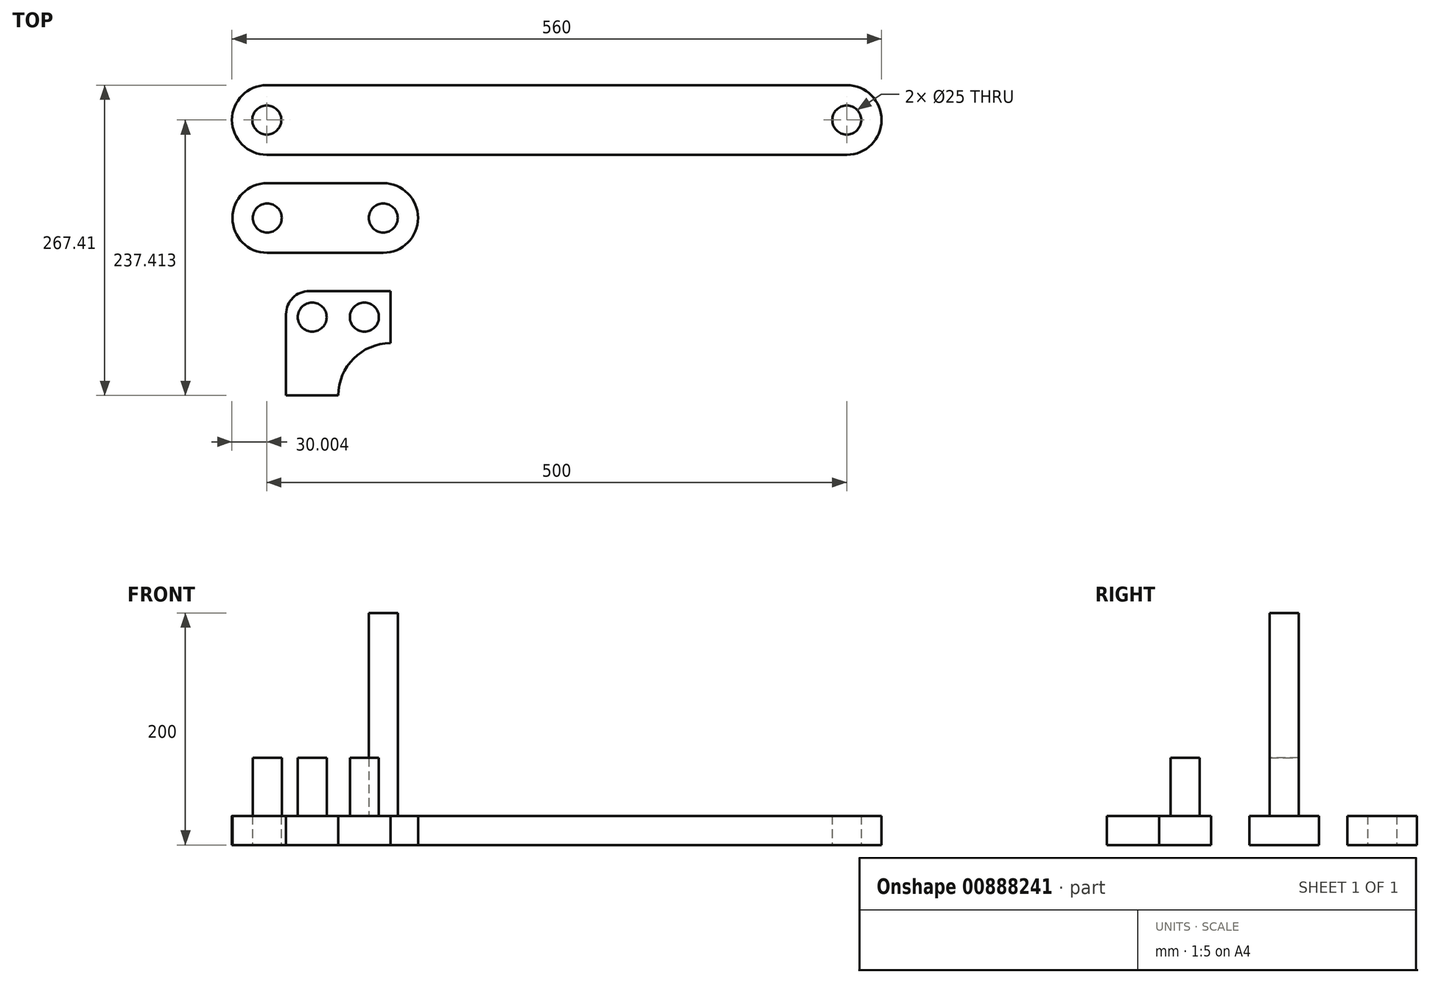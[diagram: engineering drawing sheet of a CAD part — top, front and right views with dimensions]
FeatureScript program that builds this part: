
annotation { "Feature Type Name" : "Feature", "Feature Type Description" : "" }
export const myFeature = defineFeature(function(context is Context, id is Id, definition is map)
    precondition{}
    {
        {
            var Q0;
            Q0=qCreatedBy(makeId("Top.planeOp"),FACE);
            var sketch = newSketch(context, id + "F0", { "sketchPlane" : qUnion([Q0])});
            skLineSegment(sketch, "E0.bottom", {"start": v(50, 30) * mm, "end": v(-50, 30) * mm});
            skLineSegment(sketch, "E0.top", {"start": v(50, -30) * mm, "end": v(-50, -30) * mm});
            skPoint(sketch, "E0.middle", {"position": v(0, 0) * mm});
            skPoint(sketch, "E1.center.orphan", {"position": v(-50, 0) * mm});
            skPoint(sketch, "E2.center.orphan", {"position": v(50, 0) * mm});
            skArc(sketch, "E3", {"start": v(-50, 30) * mm, "mid": v(-80, 0) * mm, "end": v(-50, -30) * mm});
            skArc(sketch, "E4", {"start": v(50, -30) * mm, "mid": v(80, 0) * mm, "end": v(50, 30) * mm});
            skCircle(sketch, "E5", {"center": v(-50, 0) * mm, "radius": 12.5 * mm});
            skCircle(sketch, "E6", {"center": v(50, 0) * mm, "radius": 12.5 * mm});
            skLineSegment(sketch, "E7.bottom", {"start": v(56.26, -62.93) * mm, "end": v(-33.74, -62.93) * mm});
            skLineSegment(sketch, "E7.top", {"start": v(56.26, -107.93) * mm, "end": v(11.26, -107.93) * mm});
            skLineSegment(sketch, "E7.left", {"start": v(56.26, -62.93) * mm, "end": v(56.26, -107.93) * mm});
            skLineSegment(sketch, "E8.top", {"start": v(11.26, -152.93) * mm, "end": v(-33.74, -152.93) * mm});
            skLineSegment(sketch, "E8.left", {"start": v(11.26, -107.93) * mm, "end": v(11.26, -152.93) * mm});
            skLineSegment(sketch, "E9", {"start": v(-33.74, -62.93) * mm, "end": v(-33.74, -152.93) * mm});
            skPoint(sketch, "E10.centerSnap0", {"position": v(-11.24, -152.93) * mm});
            skPoint(sketch, "E10.centerSnap1", {"position": v(11.26, -130.43) * mm});
            skCircle(sketch, "E11", {"center": v(33.76, -85.43) * mm, "radius": 12.5 * mm});
            skPoint(sketch, "E11.centerSnap0", {"position": v(56.26, -85.43) * mm});
            skPoint(sketch, "E11.centerSnap1", {"position": v(33.76, -107.93) * mm});
            skCircle(sketch, "E12", {"center": v(-11.24, -85.43) * mm, "radius": 12.5 * mm});
            skLineSegment(sketch, "E13.bottom", {"start": v(449.6, 114.48) * mm, "end": v(-50.4, 114.48) * mm});
            skLineSegment(sketch, "E13.top", {"start": v(449.6, 54.48) * mm, "end": v(-50.4, 54.48) * mm});
            skPoint(sketch, "E13.middle", {"position": v(199.6, 84.48) * mm});
            skPoint(sketch, "E14.center.orphan", {"position": v(-50.4, 84.48) * mm});
            skPoint(sketch, "E15.center.orphan", {"position": v(449.6, 84.48) * mm});
            skArc(sketch, "E16", {"start": v(-50.4, 114.48) * mm, "mid": v(-80.4, 84.48) * mm, "end": v(-50.4, 54.48) * mm});
            skArc(sketch, "E17", {"start": v(449.6, 54.48) * mm, "mid": v(479.6, 84.48) * mm, "end": v(449.6, 114.48) * mm});
            skCircle(sketch, "E18", {"center": v(-50.4, 84.48) * mm, "radius": 12.5 * mm});
            skCircle(sketch, "E19", {"center": v(449.6, 84.48) * mm, "radius": 12.5 * mm});
            skSolve(sketch);
        }
        {
            var Q0;
            Q0=makeQuery(id+"F0.imprint","IMPRINT",FACE,{"disambiguationData":[TD([[makeQuery(id+"F0.imprint","IMPRINT",EDGE,{"derivedFrom":sQuery(id+"F0.wireOp",EDGE,"E0.bottom")}),1.0]])]});
            extrude(context, id + "F1", {"entities" : qUnion([Q0]), "depth" : 25 * mm, "offsetDistance" : 25 * mm});
        }
        {
            var Q0;
            Q0=makeQuery(id+"F0.imprint","IMPRINT",FACE,{"disambiguationData":[TD([[makeQuery(id+"F0.imprint","IMPRINT",EDGE,{"derivedFrom":sQuery(id+"F0.wireOp",EDGE,"E6")}),1.0]])]});
            extrude(context, id + "F2", {"entities" : qUnion([Q0]), "operationType" : NewBodyOperationType.ADD, "depth" : 200 * mm, "offsetDistance" : 25 * mm});
        }
        {
            var Q0;
            Q0=makeQuery(id+"F0.imprint","IMPRINT",FACE,{"disambiguationData":[TD([[makeQuery(id+"F0.imprint","IMPRINT",EDGE,{"derivedFrom":sQuery(id+"F0.wireOp",EDGE,"E5")}),1.0]])]});
            extrude(context, id + "F3", {"entities" : qUnion([Q0]), "operationType" : NewBodyOperationType.ADD, "depth" : 75 * mm, "offsetDistance" : 25 * mm});
        }
        {
            var Q0;
            Q0=makeQuery(id+"F0.imprint","IMPRINT",FACE,{"disambiguationData":[TD([[makeQuery(id+"F0.imprint","IMPRINT",EDGE,{"derivedFrom":sQuery(id+"F0.wireOp",EDGE,"E7.bottom")}),1.0]])]});
            extrude(context, id + "F4", {"entities" : qUnion([Q0]), "depth" : 25 * mm, "offsetDistance" : 25 * mm});
        }
        {
            var Q0;
            Q0=makeQuery(id+"F4.opExtrude","SWEPT_EDGE",EDGE,{"disambiguationData":[OSD([sQuery(id+"F0.wireOp",EDGE,"E7.top"),sQuery(id+"F0.wireOp",EDGE,"E8.left")])]});
            fillet(context, id + "F5", {"entities" : qUnion([Q0]), "radius" : 45 * mm, "tangentPropagation" : true, "allowEdgeOverflow" : false});
        }
        {
            var Q0;
            Q0=makeQuery(id+"F4.opExtrude","SWEPT_EDGE",EDGE,{"disambiguationData":[OSD([sQuery(id+"F0.wireOp",EDGE,"E7.bottom"),sQuery(id+"F0.wireOp",EDGE,"E9")])]});
            fillet(context, id + "F6", {"entities" : qUnion([Q0]), "radius" : 20 * mm, "tangentPropagation" : true, "allowEdgeOverflow" : false});
        }
        {
            var Q0;
            Q0=makeQuery(id+"F0.imprint","IMPRINT",FACE,{"disambiguationData":[TD([[makeQuery(id+"F0.imprint","IMPRINT",EDGE,{"derivedFrom":sQuery(id+"F0.wireOp",EDGE,"E12")}),1.0]])]});
            var Q1;
            Q1=makeQuery(id+"F0.imprint","IMPRINT",FACE,{"disambiguationData":[TD([[makeQuery(id+"F0.imprint","IMPRINT",EDGE,{"derivedFrom":sQuery(id+"F0.wireOp",EDGE,"E11")}),1.0]])]});
            extrude(context, id + "F7", {"entities" : qUnion([Q0, Q1]), "operationType" : NewBodyOperationType.ADD, "depth" : 75 * mm, "offsetDistance" : 25 * mm});
        }
        {
            var Q0;
            Q0=makeQuery(id+"F0.imprint","IMPRINT",FACE,{"disambiguationData":[TD([[makeQuery(id+"F0.imprint","IMPRINT",EDGE,{"derivedFrom":sQuery(id+"F0.wireOp",EDGE,"E13.bottom")}),1.0]])]});
            extrude(context, id + "F8", {"entities" : qUnion([Q0]), "depth" : 25 * mm, "offsetDistance" : 25 * mm});
        }
    });
